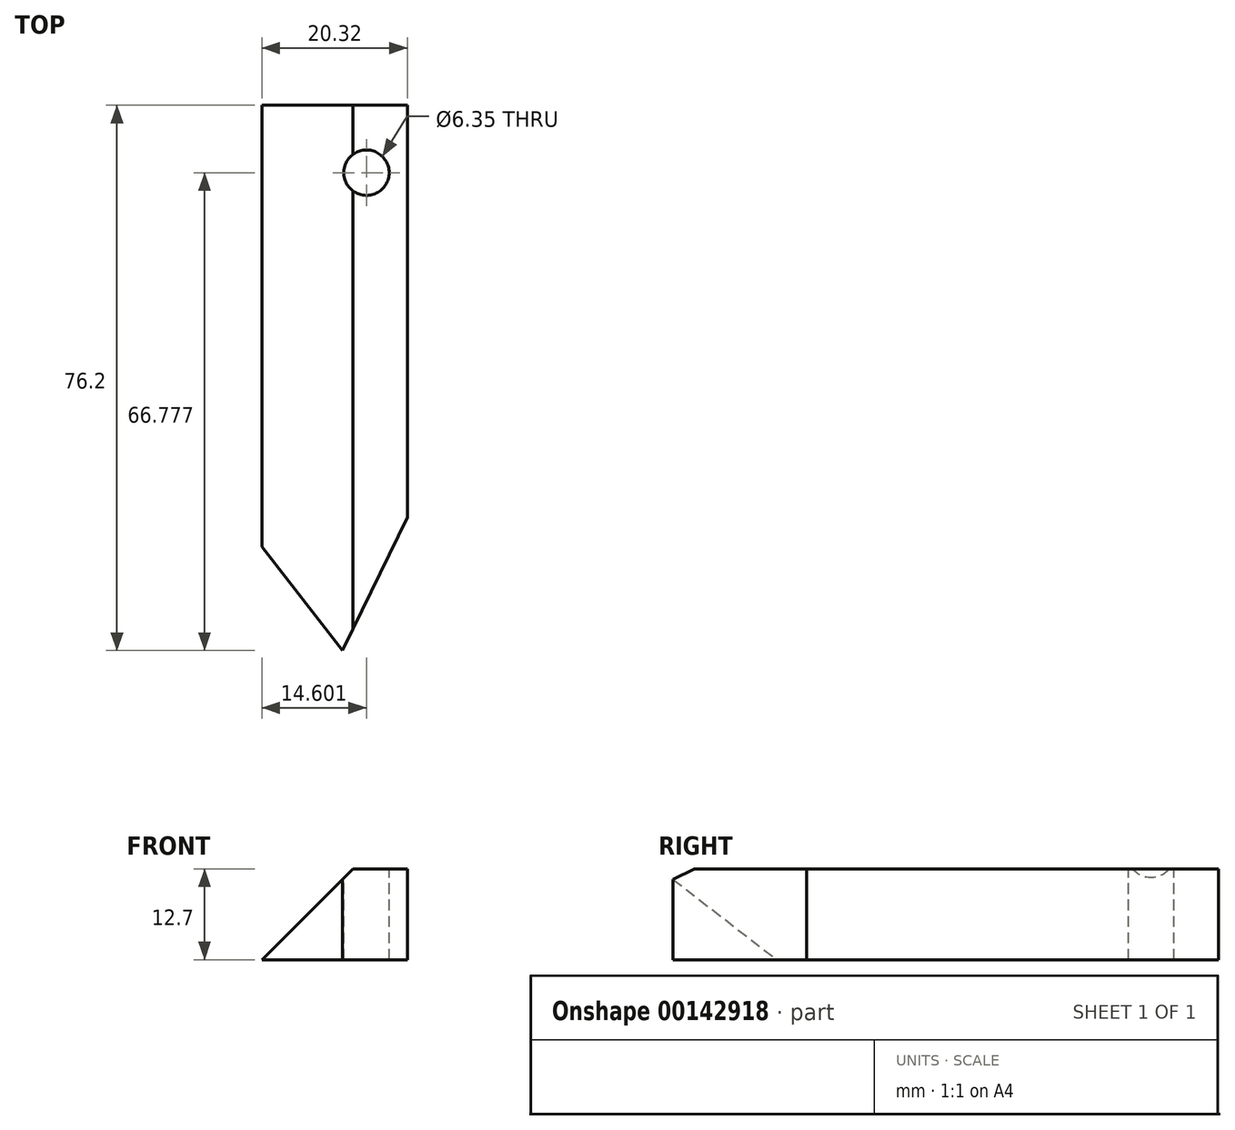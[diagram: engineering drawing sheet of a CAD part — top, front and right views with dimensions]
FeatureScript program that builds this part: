
annotation { "Feature Type Name" : "Feature", "Feature Type Description" : "" }
export const myFeature = defineFeature(function(context is Context, id is Id, definition is map)
    precondition{}
    {
        {
            var Q0;
            Q0=qCreatedBy(makeId("Top.planeOp"),FACE);
            var sketch = newSketch(context, id + "F0", { "sketchPlane" : qUnion([Q0])});
            skLineSegment(sketch, "E0", {"start": v(-11.23, 24.03) * mm, "end": v(-11.23, 0) * mm});
            skLineSegment(sketch, "E1", {"start": v(-11.23, 0) * mm, "end": v(-11.23, -37.67) * mm});
            skLineSegment(sketch, "E2", {"start": v(-11.23, -37.67) * mm, "end": v(0, -52.17) * mm});
            skLineSegment(sketch, "E3", {"start": v(0, -52.17) * mm, "end": v(9.09, -33.52) * mm});
            skLineSegment(sketch, "E4", {"start": v(9.09, -33.52) * mm, "end": v(9.09, 24.03) * mm});
            skLineSegment(sketch, "E5", {"start": v(9.09, 24.03) * mm, "end": v(-11.23, 24.03) * mm});
            skLineSegment(sketch, "E6", {"start": v(-41.52, 0) * mm, "end": v(40.85, 0) * mm, "construction": true});
            skPoint(sketch, "E7", {"position": v(0, 24.03) * mm});
            skPoint(sketch, "E8", {"position": v(0, -52.17) * mm});
            skLineSegment(sketch, "E9", {"start": v(-11.23, -37.67) * mm, "end": v(9.09, -33.52) * mm, "construction": true});
            skPoint(sketch, "E10.positionSnap0", {"position": v(-1.07, -35.6) * mm});
            skSolve(sketch);
        }
        {
            var Q0;
            Q0 = qSketchRegion(id + "F0", true);
            extrude(context, id + "F1", {"entities" : qUnion([Q0]), "depth" : 12.7 * mm});
        }
        {
            var Q0;
            Q0=makeQuery(id+"F1.opExtrude","CAP_EDGE",EDGE,{"disambiguationData":[OSD([sQuery(id+"F0.wireOp",EDGE,"E0"),sQuery(id+"F0.wireOp",EDGE,"E1")])],"isStart":false});
            chamfer(context, id + "F2", {"entities" : qUnion([Q0]), "width" : 12.7 * mm, "tangentPropagation" : true});
        }
        {
            var Q0;
            Q0=makeQuery(id+"F1.opExtrude","CAP_FACE",FACE,{"disambiguationData":[OSD([sQuery(id+"F0.wireOp",EDGE,"E0"),sQuery(id+"F0.wireOp",EDGE,"E1"),sQuery(id+"F0.wireOp",EDGE,"E2"),sQuery(id+"F0.wireOp",EDGE,"E3"),sQuery(id+"F0.wireOp",EDGE,"E4"),sQuery(id+"F0.wireOp",EDGE,"E5")])],"isStart":false});
            var sketch = newSketch(context, id + "F3", { "sketchPlane" : qUnion([Q0])});
            skCircle(sketch, "E11", {"center": v(3.37, 14.6) * mm, "radius": 3.08 * mm});
            skSolve(sketch);
        }
        {
            var Q0;
            Q0=sQuery(id+"F3.wireOp",VERTEX,"E11.center");
            var Q1;
            Q1=makeQuery(id+"F1.opExtrude","SWEPT_BODY",BODY,{"disambiguationData":[OSD([sQuery(id+"F0.wireOp",EDGE,"E0"),sQuery(id+"F0.wireOp",EDGE,"E1"),sQuery(id+"F0.wireOp",EDGE,"E2"),sQuery(id+"F0.wireOp",EDGE,"E3"),sQuery(id+"F0.wireOp",EDGE,"E4"),sQuery(id+"F0.wireOp",EDGE,"E5")])]});
            hole(context, id + "F4", {"style" : HoleStyle.SIMPLE, "endStyle" : HoleEndStyle.THROUGH, "holeDiameter" : 6.35 * mm, "locations" : qUnion([Q0]), "scope" : qUnion([Q1]), "isTappedThrough" : true});
        }
    });
